# Revit family: Пергола «Параллель» 2 Арт 15935
name_source: partatom
category: Антураж
revit_build: Autodesk Revit 2018 (Build: 20180423_1000(x64)
units: mm (PartAtom-declared; Revit-internal decimal feet)

## family parameters
Всегда вертикально = Да
Источник визуального образа = Геометрия семейства
На основе рабочей плоскости = Нет
Общий = Нет
При загрузке вырезать с полостями = Нет
Точка расчета площади = Нет

## types (2) — shared parameters
URL = https://hobbyka.ru
Артикул товара = Арт. 15935
Высота = 2000 мм
Группа модели = Навесы, перголы и ротонды
Длина = 2110 мм
Изготовитель = ООО «Хоббика»
Материал изделия = Сталь, дерево, текстиль
Цвет дивана = Ткань
Цвет каркаса = Сталь
Цвет реек = Дерево
Ширина = 2610 мм

## per-type parameters (varying)
| type | Без дополнительной перегородки | Изображение типоразмера | С перегородкой |
| Пергола «Параллель» 2. Версия с перегородкой | Нет | Пергола «Параллель» 2 Арт 15935 с перегородкой.jpg | Да |
| Пергола «Параллель» 2. Версия без дополнительной перегородки | Да | Пергола «Параллель» 2 Арт 15935 без дополнительной перегородки.jpg | Нет |

note: column(s) folded — value = type name in every type: Описание
